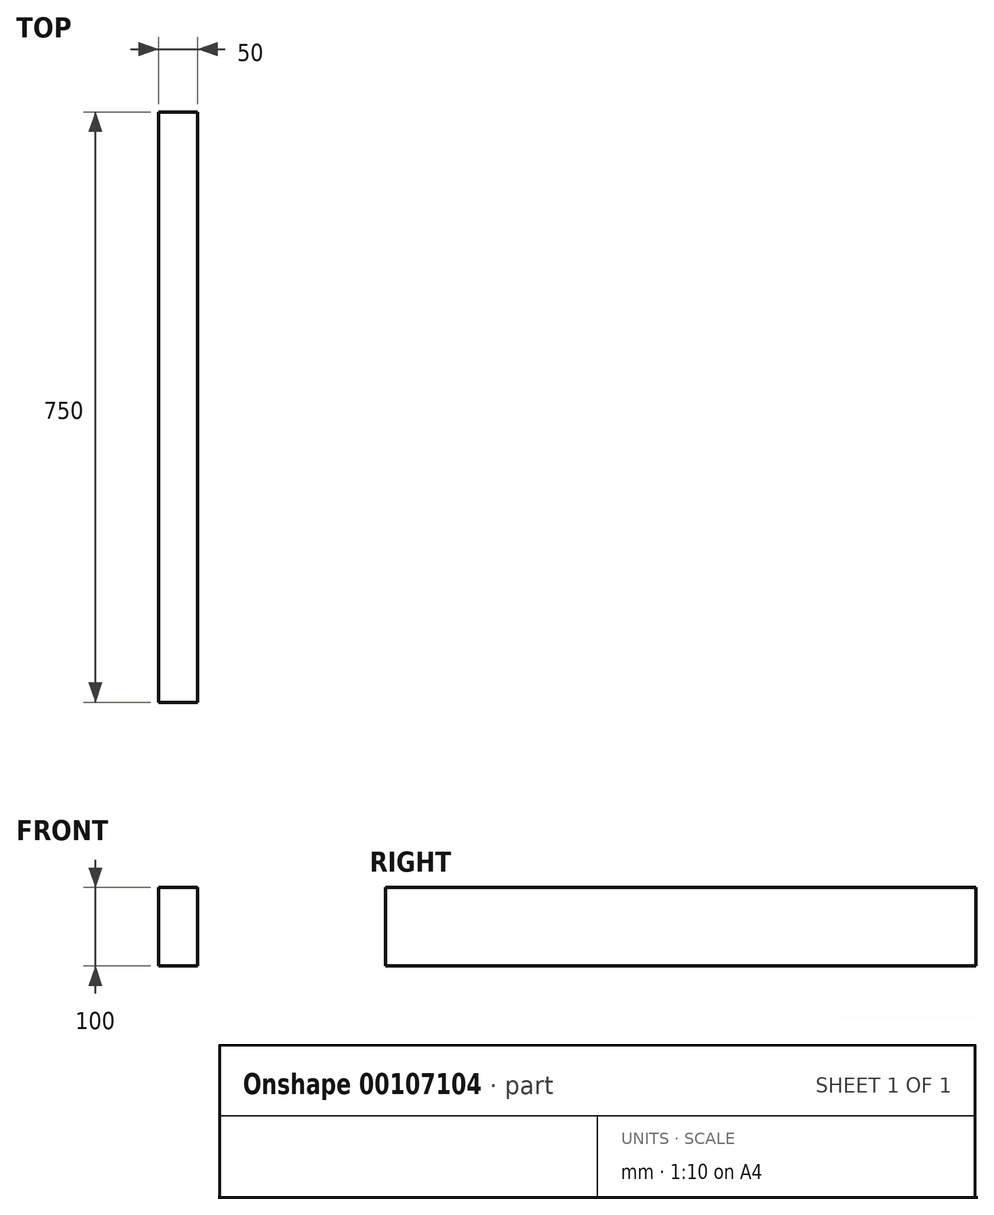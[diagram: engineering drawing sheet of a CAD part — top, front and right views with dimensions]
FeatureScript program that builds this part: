
annotation { "Feature Type Name" : "Feature", "Feature Type Description" : "" }
export const myFeature = defineFeature(function(context is Context, id is Id, definition is map)
    precondition{}
    {
        {
            var Q0;
            Q0=qCreatedBy(makeId("Front.planeOp"),FACE);
            var sketch = newSketch(context, id + "F0", { "sketchPlane" : qUnion([Q0])});
            skLineSegment(sketch, "E0.bottom", {"start": v(0, 0) * mm, "end": v(50, 0) * mm});
            skLineSegment(sketch, "E0.top", {"start": v(0, 100) * mm, "end": v(50, 100) * mm});
            skLineSegment(sketch, "E0.left", {"start": v(0, 0) * mm, "end": v(0, 100) * mm});
            skLineSegment(sketch, "E0.right", {"start": v(50, 0) * mm, "end": v(50, 100) * mm});
            skSolve(sketch);
        }
        {
            var Q0;
            Q0=qSketchRegion(id+"F0",true);
            extrude(context, id + "F1", {"entities" : qUnion([Q0]), "depth" : 750 * mm});
        }
    });
